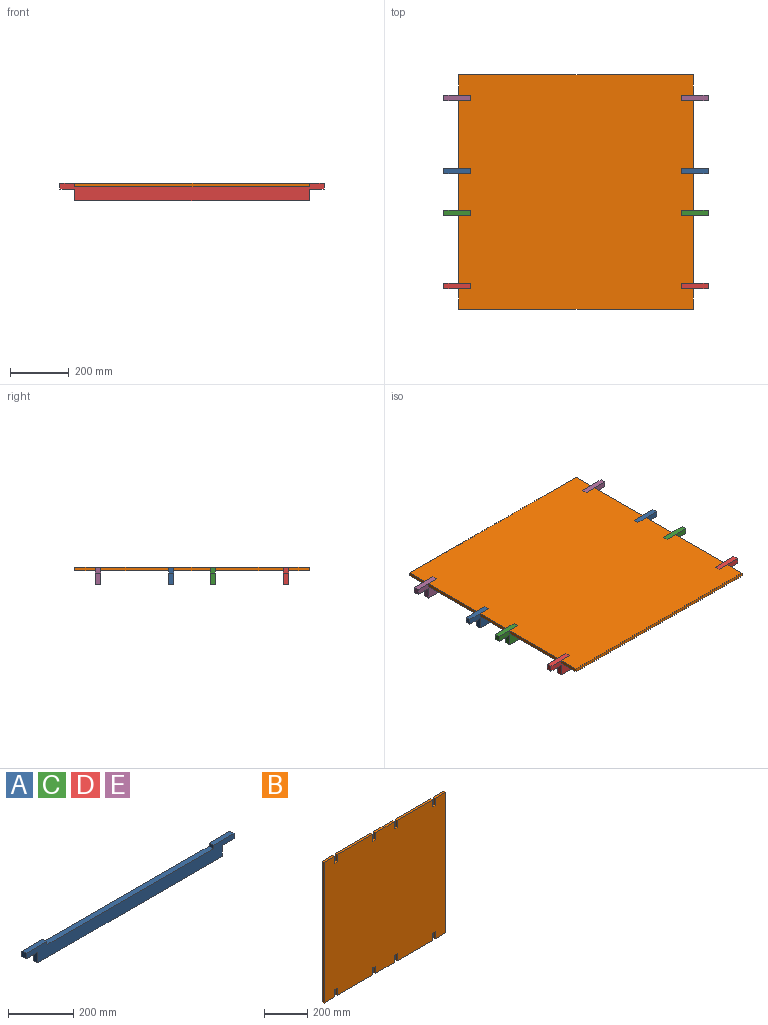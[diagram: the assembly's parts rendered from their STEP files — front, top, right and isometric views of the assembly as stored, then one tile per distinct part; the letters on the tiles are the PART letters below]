
ASSEMBLY  parts=5 mates=4
PART A: 14 faces, bbox 898x18x60 mm
  f0: plane 90x18mm, normal (0,0,1), area 1620mm2, adj f1,f11,f12,f13
  f1: plane 18x12mm, normal (-1,0,0), area 216mm2, adj f0,f2,f12,f13
  f2: plane 718x18mm, normal (0,0,1), area 12924mm2, adj f1,f3,f12,f13
  f3: plane 18x12mm, normal (1,0,0), area 216mm2, adj f2,f4,f12,f13
  f4: plane 90x18mm, normal (0,0,1), area 1620mm2, adj f3,f5,f12,f13
  f5: plane 20x18mm, normal (-1,0,0), area 360mm2, adj f4,f6,f12,f13
  f6: plane 50x18mm, normal (0,0,-1), area 900mm2, adj f5,f7,f12,f13
  f7: plane 40x18mm, normal (-1,0,0), area 720mm2, adj f6,f8,f12,f13
  f8: plane 798x18mm, normal (0,0,-1), area 14364mm2, adj f7,f9,f12,f13
  f9: plane 40x18mm, normal (1,0,0), area 720mm2, adj f8,f10,f12,f13
  f10: plane 50x18mm, normal (0,0,-1), area 900mm2, adj f9,f11,f12,f13
  f11: plane 20x18mm, normal (1,0,0), area 360mm2, adj f0,f10,f12,f13
  f12: plane 898x60mm, normal (0,-1,0), area 41264mm2, adj f0,f1,f2,f3,f4,f5,f6,f7
  f13: plane 898x60mm, normal (0,1,0), area 41264mm2, adj f0,f1,f2,f3,f4,f5,f6,f7
PART B: 38 faces, bbox 798x12x798 mm
  f0: plane 70.5x12mm, normal (0,0,1), area 846mm2, adj f1,f35,f36,f37
  f1: plane 40x12mm, normal (-1,0,0), area 480mm2, adj f0,f2,f36,f37
  f2: plane 18x12mm, normal (0,0,1), area 216mm2, adj f1,f3,f36,f37
  f3: plane 40x12mm, normal (1,0,0), area 480mm2, adj f2,f4,f36,f37
  f4: plane 231x12mm, normal (0,0,1), area 2772mm2, adj f3,f5,f36,f37
  f5: plane 40x12mm, normal (-1,0,0), area 480mm2, adj f4,f6,f36,f37
  f6: plane 18x12mm, normal (0,0,1), area 216mm2, adj f5,f7,f36,f37
  f7: plane 40x12mm, normal (1,0,0), area 480mm2, adj f6,f8,f36,f37
  f8: plane 123x12mm, normal (0,0,1), area 1476mm2, adj f7,f9,f36,f37
  f9: plane 40x12mm, normal (-1,0,0), area 480mm2, adj f8,f10,f36,f37
  f10: plane 18x12mm, normal (0,0,1), area 216mm2, adj f9,f11,f36,f37
  f11: plane 40x12mm, normal (1,0,0), area 480mm2, adj f10,f12,f36,f37
  f12: plane 231x12mm, normal (0,0,1), area 2772mm2, adj f11,f13,f36,f37
  f13: plane 40x12mm, normal (-1,0,0), area 480mm2, adj f12,f14,f36,f37
  f14: plane 18x12mm, normal (0,0,1), area 216mm2, adj f13,f15,f36,f37
  f15: plane 40x12mm, normal (1,0,0), area 480mm2, adj f14,f16,f36,f37
  f16: plane 70.5x12mm, normal (0,0,1), area 846mm2, adj f15,f17,f36,f37
  f17: plane 798x12mm, normal (-1,0,0), area 9576mm2, adj f16,f18,f36,f37
  f18: plane 70.5x12mm, normal (0,0,-1), area 846mm2, adj f17,f19,f36,f37
  f19: plane 40x12mm, normal (1,0,0), area 480mm2, adj f18,f20,f36,f37
  f20: plane 18x12mm, normal (0,0,-1), area 216mm2, adj f19,f21,f36,f37
  f21: plane 40x12mm, normal (-1,0,0), area 480mm2, adj f20,f22,f36,f37
  f22: plane 231x12mm, normal (0,0,-1), area 2772mm2, adj f21,f23,f36,f37
  f23: plane 40x12mm, normal (1,0,0), area 480mm2, adj f22,f24,f36,f37
  f24: plane 18x12mm, normal (0,0,-1), area 216mm2, adj f23,f25,f36,f37
  f25: plane 40x12mm, normal (-1,0,0), area 480mm2, adj f24,f26,f36,f37
  f26: plane 123x12mm, normal (0,0,-1), area 1476mm2, adj f25,f27,f36,f37
  f27: plane 40x12mm, normal (1,0,0), area 480mm2, adj f26,f28,f36,f37
  f28: plane 18x12mm, normal (0,0,-1), area 216mm2, adj f27,f29,f36,f37
  f29: plane 40x12mm, normal (-1,0,0), area 480mm2, adj f28,f30,f36,f37
  f30: plane 231x12mm, normal (0,0,-1), area 2772mm2, adj f29,f31,f36,f37
  f31: plane 40x12mm, normal (1,0,0), area 480mm2, adj f30,f32,f36,f37
  f32: plane 18x12mm, normal (0,0,-1), area 216mm2, adj f31,f33,f36,f37
  f33: plane 40x12mm, normal (-1,0,0), area 480mm2, adj f32,f34,f36,f37
  f34: plane 70.5x12mm, normal (0,0,-1), area 846mm2, adj f33,f35,f36,f37
  f35: plane 798x12mm, normal (1,0,0), area 9576mm2, adj f0,f34,f36,f37
  f36: plane 798x798mm, normal (0,-1,0), area 631044mm2, adj f0,f1,f2,f3,f4,f5,f6,f7
  f37: plane 798x798mm, normal (0,1,0), area 631044mm2, adj f0,f1,f2,f3,f4,f5,f6,f7
PART C: same geometry as A
PART D: same geometry as A
PART E: same geometry as A
PLACE A t=(-343.25,-625.48,-40.79)mm
PLACE B rot(axis=(0.58,0.58,0.58),120deg) t=(-293.25,-1103.98,-20.79)mm
PLACE C t=(-343.25,-766.48,-40.79)mm
PLACE D t=(-343.25,-1015.48,-40.79)mm
PLACE E t=(-343.25,-376.48,-40.79)mm
MATE fastened C.f4 <-> E.f4  axis (0,0,1) through (-343.25,-766.48,-20.79)mm
MATE fastened E.f4 <-> D.f4  axis (0,0,1) through (-343.25,-376.48,-20.79)mm
MATE fastened B.f37 <-> E.f4  axis (0,0,1) through (-253.25,-376.48,-20.79)mm
MATE fastened E.f4 <-> A.f4  axis (0,0,1) through (-343.25,-376.48,-20.79)mm
